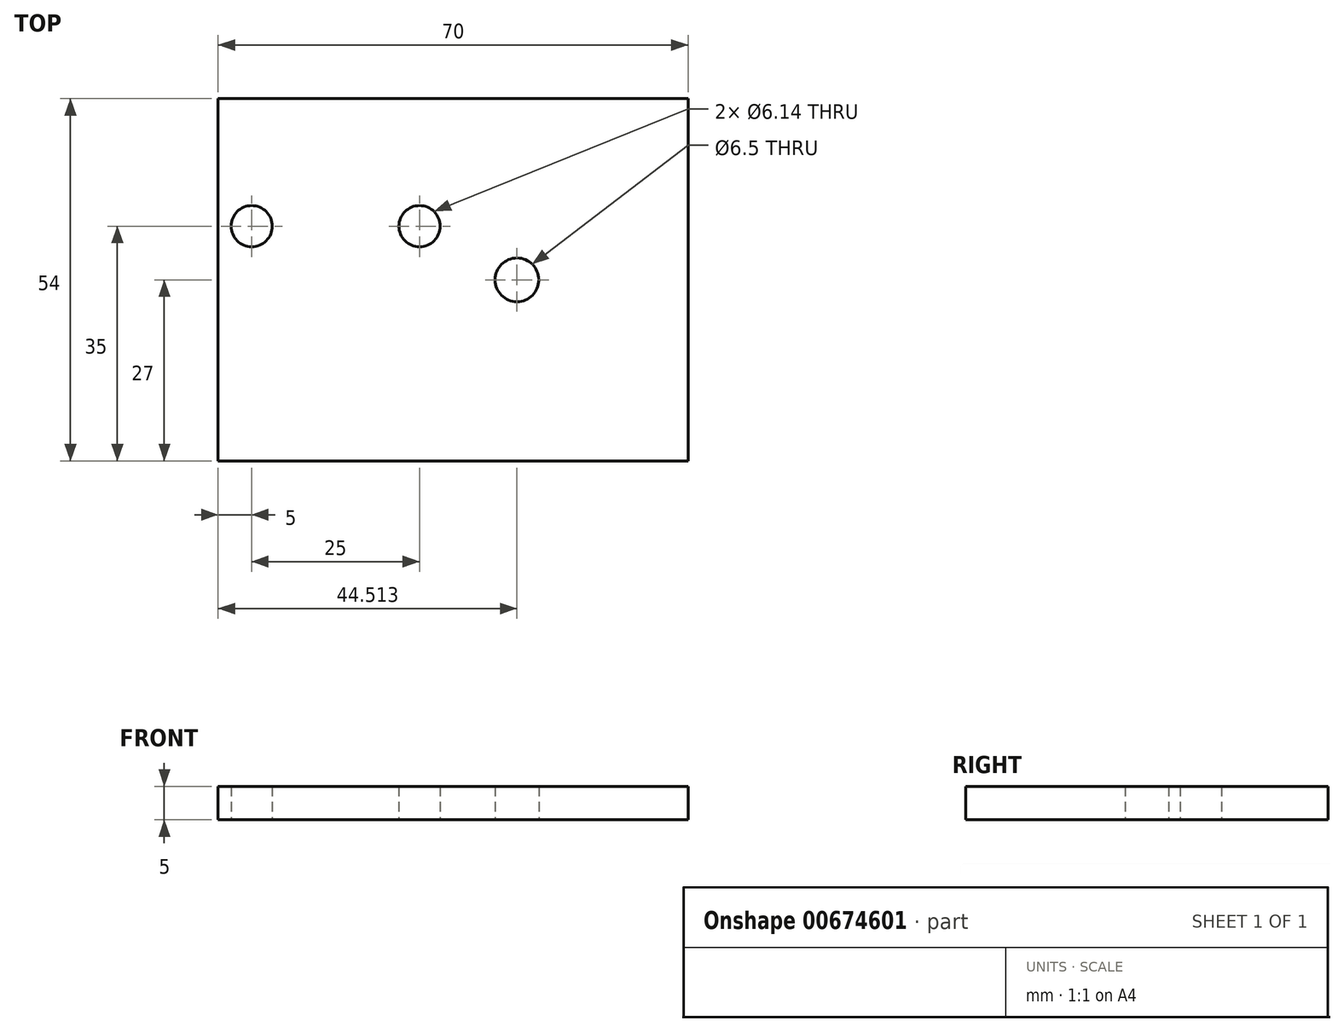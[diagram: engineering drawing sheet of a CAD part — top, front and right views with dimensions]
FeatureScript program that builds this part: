
annotation { "Feature Type Name" : "Feature", "Feature Type Description" : "" }
export const myFeature = defineFeature(function(context is Context, id is Id, definition is map)
    precondition{}
    {
        {
            var Q0;
            Q0=qCreatedBy(makeId("Top.planeOp"),FACE);
            var sketch = newSketch(context, id + "F0", { "sketchPlane" : qUnion([Q0])});
            skLineSegment(sketch, "E0.bottom", {"start": v(35, 19) * mm, "end": v(-35, 19) * mm});
            skLineSegment(sketch, "E0.top", {"start": v(35, -35) * mm, "end": v(-35, -35) * mm});
            skLineSegment(sketch, "E0.left", {"start": v(35, 19) * mm, "end": v(35, -35) * mm});
            skLineSegment(sketch, "E0.right", {"start": v(-35, 19) * mm, "end": v(-35, -35) * mm});
            skPoint(sketch, "E0.middle", {"position": v(0, -8) * mm});
            skCircle(sketch, "E1", {"center": v(-30, 0) * mm, "radius": 3.07 * mm});
            skCircle(sketch, "E2", {"center": v(-5, 0) * mm, "radius": 3.07 * mm});
            skCircle(sketch, "E3", {"center": v(9.51, -8) * mm, "radius": 3.25 * mm});
            skPoint(sketch, "E4", {"position": v(35, -8) * mm});
            skSolve(sketch);
        }
        {
            var Q0;
            Q0=makeQuery(id+"F0.imprint","IMPRINT",FACE,{"disambiguationData":[TD([[makeQuery(id+"F0.imprint","IMPRINT",EDGE,{"derivedFrom":sQuery(id+"F0.wireOp",EDGE,"E0.bottom")}),1.0]])]});
            extrude(context, id + "F1", {"entities" : qUnion([Q0]), "depth" : 5 * mm, "offsetDistance" : 25 * mm});
        }
    });
